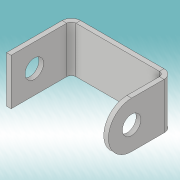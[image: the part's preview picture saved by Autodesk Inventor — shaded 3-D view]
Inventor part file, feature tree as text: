
AUTODESK INVENTOR PART (.ipt)
format: ipt  version: 2019 (Build 230136000, 136)  size: 158,720 bytes
history: native  units: in
note: dims shown in document units (in); Inventor stores cm internally (conversion verified against a paired STEP export)
features: sketch x5, sheet_metal_op x3, other x3, extrude x2
ambient origin geometry x8: Origin, YZ Plane, XZ Plane, XY Plane, X Axis, Y Axis, Z Axis, Center Point
bodies: Solid1 (feature_tree)
feature tree (13):
  extrude  "Extrusion1"  Depth=0.7874in
  sheet_metal_op  "Flange1"
  extrude  "Extrusion2"  Depth=0.0787in
  sketch  "Sketch1"  dims[d0=1.7323in d1=0.7874in]
  sketch  "Sketch2"  dims[d2=0.0787in d3=0.0in d4=0.0787in]
  other  "Plate1"
  sheet_metal_op  "Bend1"
  sheet_metal_op  "Corner1"
  sketch  "Sketch3"  dims[d5=0.0787in]
  sketch  "Sketch4"  dims[d6=0.0394in]
  sketch  "Sketch5"  dims[d7=0.1575in d8=0.0787in d9=1.1024in d10=90.0deg d11=0.0787in d12=0.315in d13=0.0787in d14=0.0787in d15=0.3937in d16=0.315in d17=0.0787in d18=0.0in d19=0.0787in d20=0.0in d21=0.3543in d22=0.7087in d23=0.3937in d24=0.0039in d25=0.0in]
  other  "Cut1"
  other  "Cut2"
